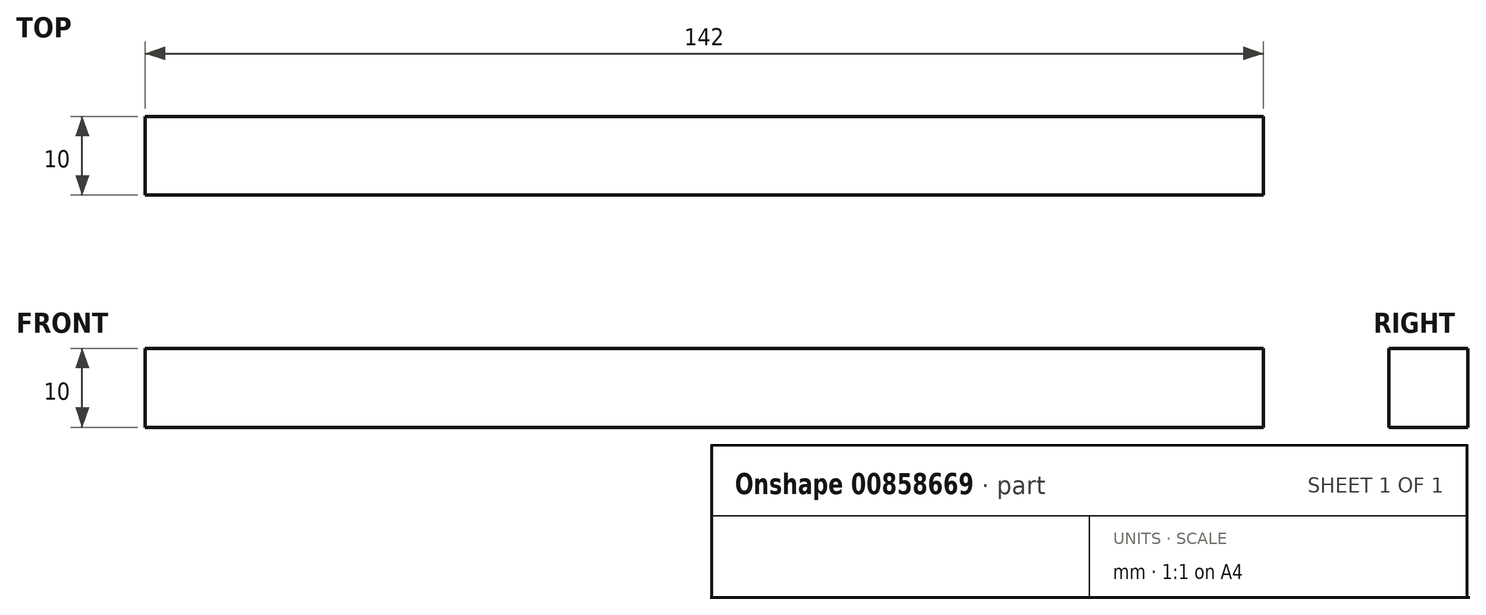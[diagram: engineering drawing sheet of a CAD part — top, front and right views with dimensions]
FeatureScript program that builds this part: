
annotation { "Feature Type Name" : "Feature", "Feature Type Description" : "" }
export const myFeature = defineFeature(function(context is Context, id is Id, definition is map)
    precondition{}
    {
        {
            var Q0;
            Q0=qCreatedBy(makeId("Right.planeOp"),FACE);
            var sketch = newSketch(context, id + "F0", { "sketchPlane" : qUnion([Q0])});
            skLineSegment(sketch, "E0.bottom", {"start": v(0, 10) * mm, "end": v(-10, 10) * mm});
            skLineSegment(sketch, "E0.top", {"start": v(0, 0) * mm, "end": v(-10, 0) * mm});
            skLineSegment(sketch, "E0.left", {"start": v(0, 10) * mm, "end": v(0, 0) * mm});
            skLineSegment(sketch, "E0.right", {"start": v(-10, 10) * mm, "end": v(-10, 0) * mm});
            skSolve(sketch);
        }
        {
            var Q0;
            Q0=makeQuery(id+"F0.imprint","IMPRINT",FACE,{"disambiguationData":[TD([[makeQuery(id+"F0.imprint","IMPRINT",EDGE,{"derivedFrom":sQuery(id+"F0.wireOp",EDGE,"E0.bottom")}),1.0]])]});
            extrude(context, id + "F1", {"entities" : qUnion([Q0]), "depth" : 142 * mm, "offsetDistance" : 25 * mm});
        }
    });
